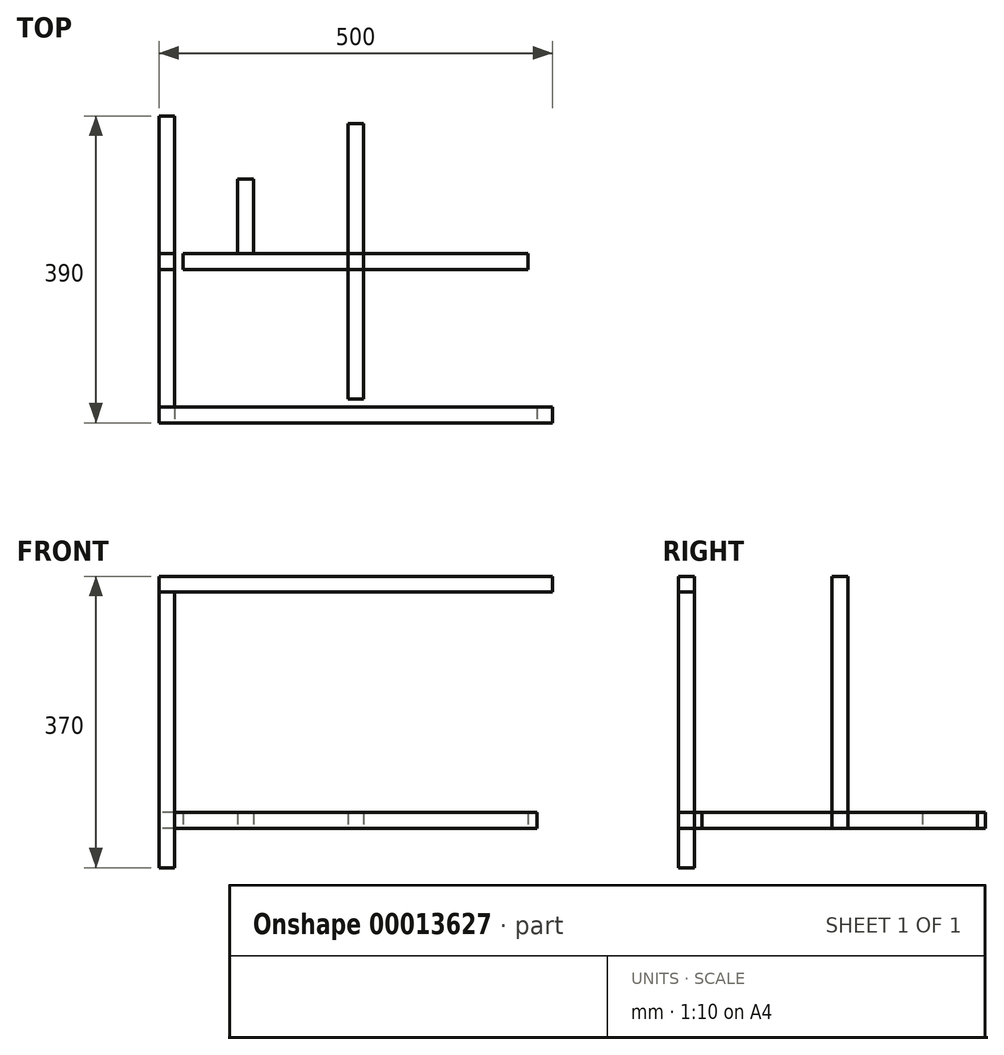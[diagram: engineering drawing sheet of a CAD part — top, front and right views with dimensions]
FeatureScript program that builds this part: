
annotation { "Feature Type Name" : "Feature", "Feature Type Description" : "" }
export const myFeature = defineFeature(function(context is Context, id is Id, definition is map)
    precondition{}
    {
        {
            var Q0;
            Q0=qCreatedBy(makeId("Top.planeOp"),FACE);
            var sketch = newSketch(context, id + "F0", { "sketchPlane" : qUnion([Q0])});
            skLineSegment(sketch, "E0.rect.bottom", {"start": v(150, 100) * mm, "end": v(-150, 100) * mm, "construction": true});
            skLineSegment(sketch, "E0.rect.top", {"start": v(150, -100) * mm, "end": v(-150, -100) * mm, "construction": true});
            skLineSegment(sketch, "E0.rect.left", {"start": v(150, 100) * mm, "end": v(150, -100) * mm});
            skLineSegment(sketch, "E0.rect.right", {"start": v(-150, 100) * mm, "end": v(-150, -100) * mm});
            skPoint(sketch, "E0.rect.middle", {"position": v(0, 0) * mm});
            skLineSegment(sketch, "E1.rect.bottom", {"start": v(219, 10) * mm, "end": v(-219, 10) * mm});
            skLineSegment(sketch, "E1.rect.top", {"start": v(219, -10) * mm, "end": v(-219, -10) * mm});
            skLineSegment(sketch, "E1.rect.left", {"start": v(219, 10) * mm, "end": v(219, -10) * mm});
            skLineSegment(sketch, "E1.rect.right", {"start": v(-219, 10) * mm, "end": v(-219, -10) * mm});
            skLineSegment(sketch, "E2.rect.bottom", {"start": v(-178, -20) * mm, "end": v(-220, -20) * mm});
            skLineSegment(sketch, "E2.rect.top", {"start": v(-178, -62) * mm, "end": v(-220, -62) * mm});
            skLineSegment(sketch, "E2.rect.left", {"start": v(-178, -20) * mm, "end": v(-178, -62) * mm});
            skLineSegment(sketch, "E2.rect.right", {"start": v(-220, -20) * mm, "end": v(-220, -62) * mm});
            skPoint(sketch, "E2.rect.middle", {"position": v(-199, -41) * mm});
            skLineSegment(sketch, "E3.rect.bottom", {"start": v(-130, -105) * mm, "end": v(-150, -105) * mm});
            skLineSegment(sketch, "E3.rect.top", {"start": v(-130, 105) * mm, "end": v(-150, 105) * mm});
            skLineSegment(sketch, "E3.rect.left", {"start": v(-130, -105) * mm, "end": v(-130, 105) * mm});
            skLineSegment(sketch, "E3.rect.right", {"start": v(-150, -105) * mm, "end": v(-150, 105) * mm});
            skPoint(sketch, "E3.rect.middle", {"position": v(-140, 0) * mm});
            skLineSegment(sketch, "E4", {"start": v(0, 0) * mm, "end": v(0, -201.7) * mm, "construction": true});
            skLineSegment(sketch, "E5.0.MirrorCS", {"start": v(178, -62) * mm, "end": v(220, -62) * mm});
            skLineSegment(sketch, "E6.0.MirrorCS", {"start": v(178, -20) * mm, "end": v(178, -62) * mm});
            skLineSegment(sketch, "E7.0.MirrorCS", {"start": v(178, -20) * mm, "end": v(220, -20) * mm});
            skLineSegment(sketch, "E8.0.MirrorCS", {"start": v(220, -20) * mm, "end": v(220, -62) * mm});
            skLineSegment(sketch, "E9.0.MirrorCS", {"start": v(130, -105) * mm, "end": v(130, 105) * mm});
            skLineSegment(sketch, "E10.0.MirrorCS", {"start": v(130, -105) * mm, "end": v(150, -105) * mm});
            skLineSegment(sketch, "E11.0.MirrorCS", {"start": v(150, -105) * mm, "end": v(150, 105) * mm});
            skLineSegment(sketch, "E12.0.MirrorCS", {"start": v(130, 105) * mm, "end": v(150, 105) * mm});
            skLineSegment(sketch, "E13.rect.bottom", {"start": v(-230, 185) * mm, "end": v(230, 185) * mm});
            skLineSegment(sketch, "E13.rect.top", {"start": v(-230, -185) * mm, "end": v(230, -185) * mm});
            skLineSegment(sketch, "E13.rect.left", {"start": v(-230, 185) * mm, "end": v(-230, -185) * mm});
            skLineSegment(sketch, "E13.rect.right", {"start": v(230, 185) * mm, "end": v(230, -185) * mm});
            skLineSegment(sketch, "E14.rect.bottom", {"start": v(-250, 205) * mm, "end": v(250, 205) * mm});
            skLineSegment(sketch, "E14.rect.top", {"start": v(-250, -205) * mm, "end": v(250, -205) * mm});
            skLineSegment(sketch, "E14.rect.left", {"start": v(-250, 205) * mm, "end": v(-250, -205) * mm});
            skLineSegment(sketch, "E14.rect.right", {"start": v(250, 205) * mm, "end": v(250, -205) * mm});
            skLineSegment(sketch, "E15", {"start": v(-230, 185) * mm, "end": v(-230, 205) * mm});
            skLineSegment(sketch, "E16", {"start": v(-230, 185) * mm, "end": v(-250, 185) * mm});
            skLineSegment(sketch, "E17", {"start": v(230, 185) * mm, "end": v(250, 185) * mm});
            skLineSegment(sketch, "E18", {"start": v(230, 185) * mm, "end": v(230, 205) * mm});
            skLineSegment(sketch, "E19", {"start": v(230, -185) * mm, "end": v(250, -185) * mm});
            skLineSegment(sketch, "E20", {"start": v(230, -185) * mm, "end": v(230, -205) * mm});
            skLineSegment(sketch, "E21", {"start": v(-230, -185) * mm, "end": v(-230, -205) * mm});
            skLineSegment(sketch, "E22", {"start": v(-230, -185) * mm, "end": v(-250, -185) * mm});
            skCircle(sketch, "E23", {"center": v(-199, -41) * mm, "radius": 12.5 * mm});
            skCircle(sketch, "E24.0.MirrorC", {"center": v(199, -41) * mm, "radius": 12.5 * mm});
            skLineSegment(sketch, "E25.rect.bottom", {"start": v(-10, 175) * mm, "end": v(10, 175) * mm});
            skLineSegment(sketch, "E25.rect.top", {"start": v(-10, -175) * mm, "end": v(10, -175) * mm});
            skLineSegment(sketch, "E25.rect.left", {"start": v(-10, 175) * mm, "end": v(-10, -175) * mm});
            skLineSegment(sketch, "E25.rect.right", {"start": v(10, 175) * mm, "end": v(10, -175) * mm});
            skSolve(sketch);
        }
        {
            var Q0;
            Q0=sQuery(id+"F0.wireOp",EDGE,"E14.rect.top");
            cPlane(context, id + "F1", {"entities" : qUnion([Q0]), "cplaneType" : CPlaneType.LINE_ANGLE, "offset" : 150 * mm, "angle" : 0 * degree, "width" : 150 * mm, "height" : 150 * mm});
        }
        {
            var Q0;
            Q0=qCreatedBy(id+"F1.planeOp",FACE);
            var sketch = newSketch(context, id + "F2", { "sketchPlane" : qUnion([Q0])});
            skPoint(sketch, "E26.0", {"position": v(230, 0) * mm});
            skPoint(sketch, "E27.0", {"position": v(250, 0) * mm});
            skPoint(sketch, "E28.0", {"position": v(-230, 0) * mm});
            skPoint(sketch, "E29.0", {"position": v(-250, 0) * mm});
            skLineSegment(sketch, "E30", {"start": v(230, 0) * mm, "end": v(230, 300) * mm});
            skLineSegment(sketch, "E31", {"start": v(230, 300) * mm, "end": v(250, 300) * mm});
            skLineSegment(sketch, "E32", {"start": v(250, 300) * mm, "end": v(250, 0) * mm});
            skLineSegment(sketch, "E33", {"start": v(250, 0) * mm, "end": v(250, -50) * mm});
            skLineSegment(sketch, "E34", {"start": v(250, -50) * mm, "end": v(230, -50) * mm});
            skLineSegment(sketch, "E35", {"start": v(230, -50) * mm, "end": v(230, 0) * mm});
            skLineSegment(sketch, "E36", {"start": v(-230, 0) * mm, "end": v(-230, 300) * mm});
            skLineSegment(sketch, "E37", {"start": v(-230, 300) * mm, "end": v(-250, 300) * mm});
            skLineSegment(sketch, "E38", {"start": v(230, 300) * mm, "end": v(-230, 300) * mm});
            skLineSegment(sketch, "E39", {"start": v(230, 0) * mm, "end": v(-230, 0) * mm});
            skLineSegment(sketch, "E40", {"start": v(-230, 20) * mm, "end": v(230, 20) * mm});
            skLineSegment(sketch, "E41", {"start": v(-250, 0) * mm, "end": v(-250, 300) * mm});
            skLineSegment(sketch, "E42", {"start": v(-230, 0) * mm, "end": v(-230, -50) * mm});
            skLineSegment(sketch, "E43", {"start": v(-230, -50) * mm, "end": v(-250, -50) * mm});
            skLineSegment(sketch, "E44", {"start": v(-250, -50) * mm, "end": v(-250, 0) * mm});
            skLineSegment(sketch, "E45", {"start": v(250, 320) * mm, "end": v(-250, 320) * mm});
            skLineSegment(sketch, "E46", {"start": v(-250, 320) * mm, "end": v(-250, 300) * mm});
            skLineSegment(sketch, "E47", {"start": v(250, 320) * mm, "end": v(250, 300) * mm});
            skLineSegment(sketch, "E48", {"start": v(250, 320) * mm, "end": v(250, 340) * mm});
            skLineSegment(sketch, "E49", {"start": v(250, 340) * mm, "end": v(-250, 340) * mm});
            skLineSegment(sketch, "E50", {"start": v(-250, 340) * mm, "end": v(-250, 320) * mm});
            skSolve(sketch);
        }
        {
            var Q0;
            {var subQ0=sQuery(id+"F2.wireOp",EDGE,"E31");Q0=makeQuery(id+"F2.imprint","IMPRINT",FACE,{"disambiguationData":[TD([[makeQuery(id+"F2.imprint","IMPRINT",EDGE,{"derivedFrom":subQ0}),-1.0]])]});}
            extrude(context, id + "F3", {"entities" : qUnion([Q0]), "depth" : 20 * mm});
        }
        {
            var Q0;
            {var subQ1=sQuery(id+"F2.wireOp",EDGE,"E39");Q0=makeQuery(id+"F2.imprint","IMPRINT",FACE,{"disambiguationData":[TD([[makeQuery(id+"F2.imprint","IMPRINT",EDGE,{"derivedFrom":subQ1}),-1.0]])]});}
            extrude(context, id + "F4", {"entities" : qUnion([Q0]), "depth" : 20 * mm});
        }
        {
            var Q0;
            Q0=makeQuery(id+"F0.imprint","IMPRINT",FACE,{"disambiguationData":[TD([[makeQuery(id+"F0.imprint","IMPRINT",EDGE,{"derivedFrom":sQuery(id+"F0.wireOp",EDGE,"E13.rect.left")}),-1.0]])]});
            extrude(context, id + "F5", {"entities" : qUnion([Q0]), "depth" : 20 * mm});
        }
        {
            var Q0;
            Q0=makeQuery(id+"F2.imprint","IMPRINT",FACE,{"disambiguationData":[TD([[makeQuery(id+"F2.imprint","IMPRINT",EDGE,{"derivedFrom":sQuery(id+"F2.wireOp",EDGE,"E31")}),1.0]])]});
            extrude(context, id + "F6", {"entities" : qUnion([Q0]), "depth" : 20 * mm});
        }
        {
            var Q0;
            {var subQ3=sQuery(id+"F0.wireOp",EDGE,"E25.rect.bottom");Q0=makeQuery(id+"F0.imprint","IMPRINT",FACE,{"disambiguationData":[TD([[makeQuery(id+"F0.imprint","IMPRINT",EDGE,{"derivedFrom":subQ3}),-1.0]])]});}
            var Q1;
            {var subQ0=sQuery(id+"F0.wireOp",EDGE,"E25.rect.right");var subQ3=sQuery(id+"F0.wireOp",EDGE,"E1.rect.bottom");var subQ4=makeQuery(id+"F0.imprint","INTERSECT",VERTEX,{"derivedFrom":[subQ3,subQ0]});Q1=makeQuery(id+"F0.imprint","IMPRINT",FACE,{"disambiguationData":[TD([[makeQuery(id+"F0.imprint","IMPRINT",EDGE,{"disambiguationData":[TD([[subQ4,-1.0]])],"derivedFrom":subQ3}),1.0]])]});}
            var Q2;
            {var subQ3=sQuery(id+"F0.wireOp",EDGE,"E25.rect.top");Q2=makeQuery(id+"F0.imprint","IMPRINT",FACE,{"disambiguationData":[TD([[makeQuery(id+"F0.imprint","IMPRINT",EDGE,{"derivedFrom":subQ3}),1.0]])]});}
            extrude(context, id + "F7", {"entities" : qUnion([Q0, Q1, Q2]), "depth" : 20 * mm});
        }
        {
            var Q0;
            Q0=makeQuery(id+"F5.opExtrude","CAP_FACE",FACE,{"disambiguationData":[OSD([sQuery(id+"F0.wireOp",EDGE,"E13.rect.left"),sQuery(id+"F0.wireOp",EDGE,"E14.rect.left"),sQuery(id+"F0.wireOp",EDGE,"E16"),sQuery(id+"F0.wireOp",EDGE,"E22")])],"isStart":false});
            var sketch = newSketch(context, id + "F8", { "sketchPlane" : qUnion([Q0])});
            skLineSegment(sketch, "E51", {"start": v(-230, 0) * mm, "end": v(-250, 0) * mm, "construction": true});
            skLineSegment(sketch, "E52.rect.bottom", {"start": v(-230, -10) * mm, "end": v(-250, -10) * mm});
            skLineSegment(sketch, "E52.rect.top", {"start": v(-230, 10) * mm, "end": v(-250, 10) * mm});
            skLineSegment(sketch, "E52.rect.left", {"start": v(-230, -10) * mm, "end": v(-230, 10) * mm});
            skLineSegment(sketch, "E52.rect.right", {"start": v(-250, -10) * mm, "end": v(-250, 10) * mm});
            skPoint(sketch, "E52.rect.middle", {"position": v(-240, 0) * mm});
            skSolve(sketch);
        }
        {
            var Q0;
            Q0=makeQuery(id+"F8.imprint","IMPRINT",FACE,{"disambiguationData":[TD([[makeQuery(id+"F8.imprint","IMPRINT",EDGE,{"derivedFrom":sQuery(id+"F8.wireOp",EDGE,"E52.rect.bottom")}),-1.0]])]});
            extrude(context, id + "F9", {"entities" : qUnion([Q0]), "depth" : 300 * mm});
        }
        {
            var Q0;
            {var subQ5=sQuery(id+"F0.wireOp",EDGE,"E1.rect.right");Q0=makeQuery(id+"F0.imprint","IMPRINT",FACE,{"disambiguationData":[TD([[makeQuery(id+"F0.imprint","IMPRINT",EDGE,{"derivedFrom":subQ5}),1.0]])]});}
            var Q1;
            {var subQ3=sQuery(id+"F0.wireOp",EDGE,"E1.rect.bottom");var subQ5=sQuery(id+"F0.wireOp",EDGE,"E3.rect.left");var subQ7=makeQuery(id+"F0.imprint","INTERSECT",VERTEX,{"derivedFrom":[subQ3,subQ5]});Q1=makeQuery(id+"F0.imprint","IMPRINT",FACE,{"disambiguationData":[TD([[makeQuery(id+"F0.imprint","IMPRINT",EDGE,{"disambiguationData":[TD([[subQ7,-1.0]])],"derivedFrom":subQ3}),1.0]])]});}
            var Q2;
            {var subQ0=sQuery(id+"F0.wireOp",EDGE,"E25.rect.left");var subQ3=sQuery(id+"F0.wireOp",EDGE,"E1.rect.bottom");var subQ4=makeQuery(id+"F0.imprint","INTERSECT",VERTEX,{"derivedFrom":[subQ3,subQ0]});Q2=makeQuery(id+"F0.imprint","IMPRINT",FACE,{"disambiguationData":[TD([[makeQuery(id+"F0.imprint","IMPRINT",EDGE,{"disambiguationData":[TD([[subQ4,-1.0]])],"derivedFrom":subQ3}),1.0]])]});}
            var Q3;
            {var subQ0=sQuery(id+"F0.wireOp",EDGE,"E25.rect.right");var subQ3=sQuery(id+"F0.wireOp",EDGE,"E1.rect.bottom");var subQ4=makeQuery(id+"F0.imprint","INTERSECT",VERTEX,{"derivedFrom":[subQ3,subQ0]});Q3=makeQuery(id+"F0.imprint","IMPRINT",FACE,{"disambiguationData":[TD([[makeQuery(id+"F0.imprint","IMPRINT",EDGE,{"disambiguationData":[TD([[subQ4,-1.0]])],"derivedFrom":subQ3}),1.0]])]});}
            var Q4;
            {var subQ3=sQuery(id+"F0.wireOp",EDGE,"E1.rect.bottom");var subQ5=sQuery(id+"F0.wireOp",EDGE,"E9.0.MirrorCS");var subQ7=makeQuery(id+"F0.imprint","INTERSECT",VERTEX,{"derivedFrom":[subQ3,subQ5]});Q4=makeQuery(id+"F0.imprint","IMPRINT",FACE,{"disambiguationData":[TD([[makeQuery(id+"F0.imprint","IMPRINT",EDGE,{"disambiguationData":[TD([[subQ7,-1.0]])],"derivedFrom":subQ3}),1.0]])]});}
            var Q5;
            {var subQ0=sQuery(id+"F0.wireOp",EDGE,"E11.0.MirrorCS");var subQ3=sQuery(id+"F0.wireOp",EDGE,"E1.rect.bottom");var subQ4=makeQuery(id+"F0.imprint","INTERSECT",VERTEX,{"derivedFrom":[subQ3,subQ0]});Q5=makeQuery(id+"F0.imprint","IMPRINT",FACE,{"disambiguationData":[TD([[makeQuery(id+"F0.imprint","IMPRINT",EDGE,{"disambiguationData":[TD([[subQ4,-1.0]])],"derivedFrom":subQ3}),1.0]])]});}
            var Q6;
            {var subQ5=sQuery(id+"F0.wireOp",EDGE,"E1.rect.left");Q6=makeQuery(id+"F0.imprint","IMPRINT",FACE,{"disambiguationData":[TD([[makeQuery(id+"F0.imprint","IMPRINT",EDGE,{"derivedFrom":subQ5}),-1.0]])]});}
            extrude(context, id + "F10", {"entities" : qUnion([Q0, Q1, Q2, Q3, Q4, Q5, Q6]), "depth" : 20 * mm});
        }
        {
            var Q0;
            {var subQ2=sQuery(id+"F0.wireOp",EDGE,"E3.rect.top");Q0=makeQuery(id+"F0.imprint","IMPRINT",FACE,{"disambiguationData":[TD([[makeQuery(id+"F0.imprint","IMPRINT",EDGE,{"derivedFrom":subQ2}),1.0]])]});}
            extrude(context, id + "F11", {"entities" : qUnion([Q0]), "depth" : 20 * mm});
        }
    });
